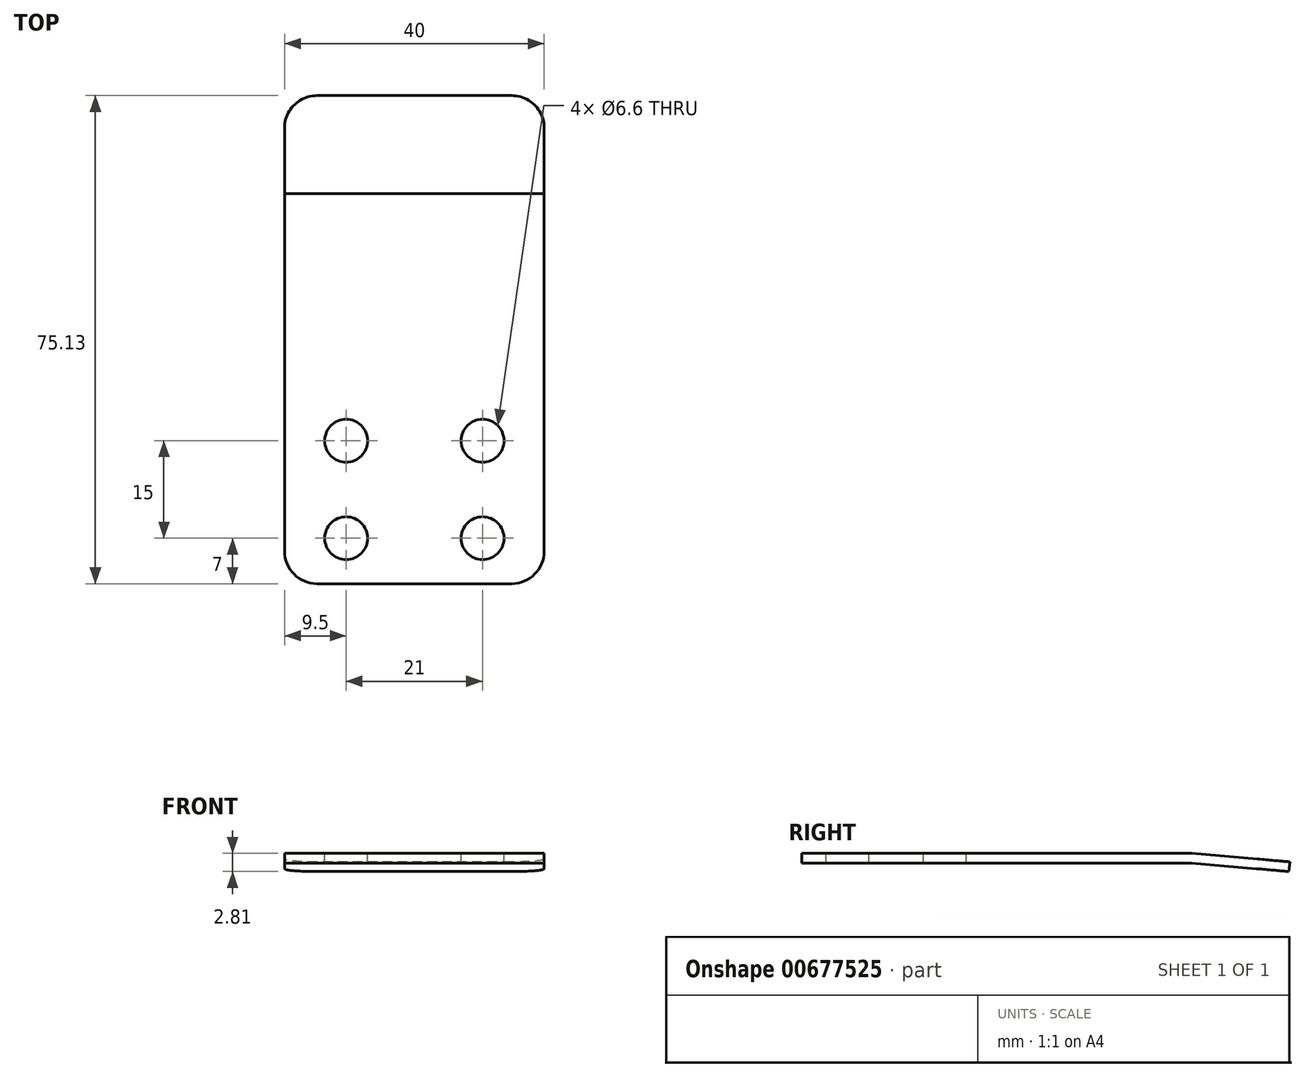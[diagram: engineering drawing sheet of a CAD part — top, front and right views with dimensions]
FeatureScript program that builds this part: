
annotation { "Feature Type Name" : "Feature", "Feature Type Description" : "" }
export const myFeature = defineFeature(function(context is Context, id is Id, definition is map)
    precondition{}
    {
        {
            var Q0;
            Q0=qCreatedBy(makeId("Right.planeOp"),FACE);
            var sketch = newSketch(context, id + "F0", { "sketchPlane" : qUnion([Q0])});
            skLineSegment(sketch, "E0", {"start": v(0, -0.75) * mm, "end": v(60, -0.75) * mm});
            skLineSegment(sketch, "E1", {"start": v(60, -0.75) * mm, "end": v(75, -2.06) * mm});
            skLineSegment(sketch, "E2", {"start": v(0, 0) * mm, "end": v(0, 60.03) * mm, "construction": true});
            skLineSegment(sketch, "E3", {"start": v(0, 0) * mm, "end": v(0, -0.75) * mm});
            skLineSegment(sketch, "E4.0", {"start": v(60.07, 0.75) * mm, "end": v(75.13, -0.57) * mm});
            skLineSegment(sketch, "E4.1", {"start": v(0, 0.75) * mm, "end": v(60.07, 0.75) * mm});
            skLineSegment(sketch, "E5", {"start": v(75.13, -0.57) * mm, "end": v(75, -2.06) * mm});
            skLineSegment(sketch, "E6", {"start": v(0, 0.75) * mm, "end": v(0, -0.75) * mm});
            skSolve(sketch);
        }
        {
            var Q0;
            Q0=makeQuery(id+"F0.imprint","IMPRINT",FACE,{"disambiguationData":[TD([[makeQuery(id+"F0.imprint","IMPRINT",EDGE,{"derivedFrom":sQuery(id+"F0.wireOp",EDGE,"E0")}),1.0]])]});
            extrude(context, id + "F1", {"entities" : qUnion([Q0]), "depth" : 40 * mm, "offsetDistance" : 25 * mm, "symmetric" : true});
        }
        {
            var Q0;
            Q0=makeQuery(id+"F1.opExtrude","SWEPT_FACE",FACE,{"disambiguationData":[OSD([sQuery(id+"F0.wireOp",EDGE,"E4.1")])]});
            var sketch = newSketch(context, id + "F2", { "sketchPlane" : qUnion([Q0])});
            skPoint(sketch, "E7", {"position": v(-10.5, 7) * mm});
            skPoint(sketch, "E8", {"position": v(-10.5, 22) * mm});
            skPoint(sketch, "E9", {"position": v(10.5, 7) * mm});
            skPoint(sketch, "E10", {"position": v(10.5, 22) * mm});
            skLineSegment(sketch, "E11", {"start": v(-10.5, 7) * mm, "end": v(10.5, 7) * mm, "construction": true});
            skPoint(sketch, "E12", {"position": v(0, 7) * mm});
            skSolve(sketch);
        }
        {
            var Q0;
            Q0=sQuery(id+"F2.wireOp",VERTEX,"E7");
            var Q1;
            Q1=sQuery(id+"F2.wireOp",VERTEX,"E9");
            var Q2;
            Q2=sQuery(id+"F2.wireOp",VERTEX,"E10");
            var Q3;
            Q3=sQuery(id+"F2.wireOp",VERTEX,"E8");
            var Q4;
            Q4=makeQuery(id+"F1.opExtrude","SWEPT_BODY",BODY,{"disambiguationData":[OSD([sQuery(id+"F0.wireOp",EDGE,"E0"),sQuery(id+"F0.wireOp",EDGE,"E1"),sQuery(id+"F0.wireOp",EDGE,"E4.0"),sQuery(id+"F0.wireOp",EDGE,"E4.1"),sQuery(id+"F0.wireOp",EDGE,"E5"),sQuery(id+"F0.wireOp",EDGE,"E6")])]});
            hole(context, id + "F3", {"style" : HoleStyle.SIMPLE, "endStyle" : HoleEndStyle.BLIND, "standardTappedOrClearance" : lookupTablePath({ "standard" : "ISO", "fit" : "Normal", "size" : "M6", "type" : "Clearance" }), "standardBlindInLast" : lookupTablePath({ "fit" : "Standard", "standard" : "ISO", "size" : "M6", "type" : "Clearance" }), "holeDiameter" : 6.6 * mm, "majorDiameter" : 6 * mm, "holeDepth" : 43 * mm, "isTappedThrough" : true, "tappedDepth" : 40 * mm, "tapClearance" : 3, "startFromSketch" : true, "locations" : qUnion([Q0, Q1, Q2, Q3]), "scope" : qUnion([Q4])});
        }
        {
            var Q0;
            Q0=makeQuery(id+"F1.opExtrude","CAP_EDGE",EDGE,{"disambiguationData":[OSD([sQuery(id+"F0.wireOp",EDGE,"E5")])],"isStart":false});
            var Q1;
            Q1=makeQuery(id+"F1.opExtrude","CAP_EDGE",EDGE,{"disambiguationData":[OSD([sQuery(id+"F0.wireOp",EDGE,"E5")])],"isStart":true});
            var Q2;
            Q2=makeQuery(id+"F1.opExtrude","CAP_EDGE",EDGE,{"disambiguationData":[OSD([sQuery(id+"F0.wireOp",EDGE,"E6")])],"isStart":false});
            var Q3;
            Q3=makeQuery(id+"F1.opExtrude","CAP_EDGE",EDGE,{"disambiguationData":[OSD([sQuery(id+"F0.wireOp",EDGE,"E6")])],"isStart":true});
            fillet(context, id + "F4", {"entities" : qUnion([Q0, Q1, Q2, Q3]), "radius" : 5 * mm, "tangentPropagation" : true, "allowEdgeOverflow" : false});
        }
    });
